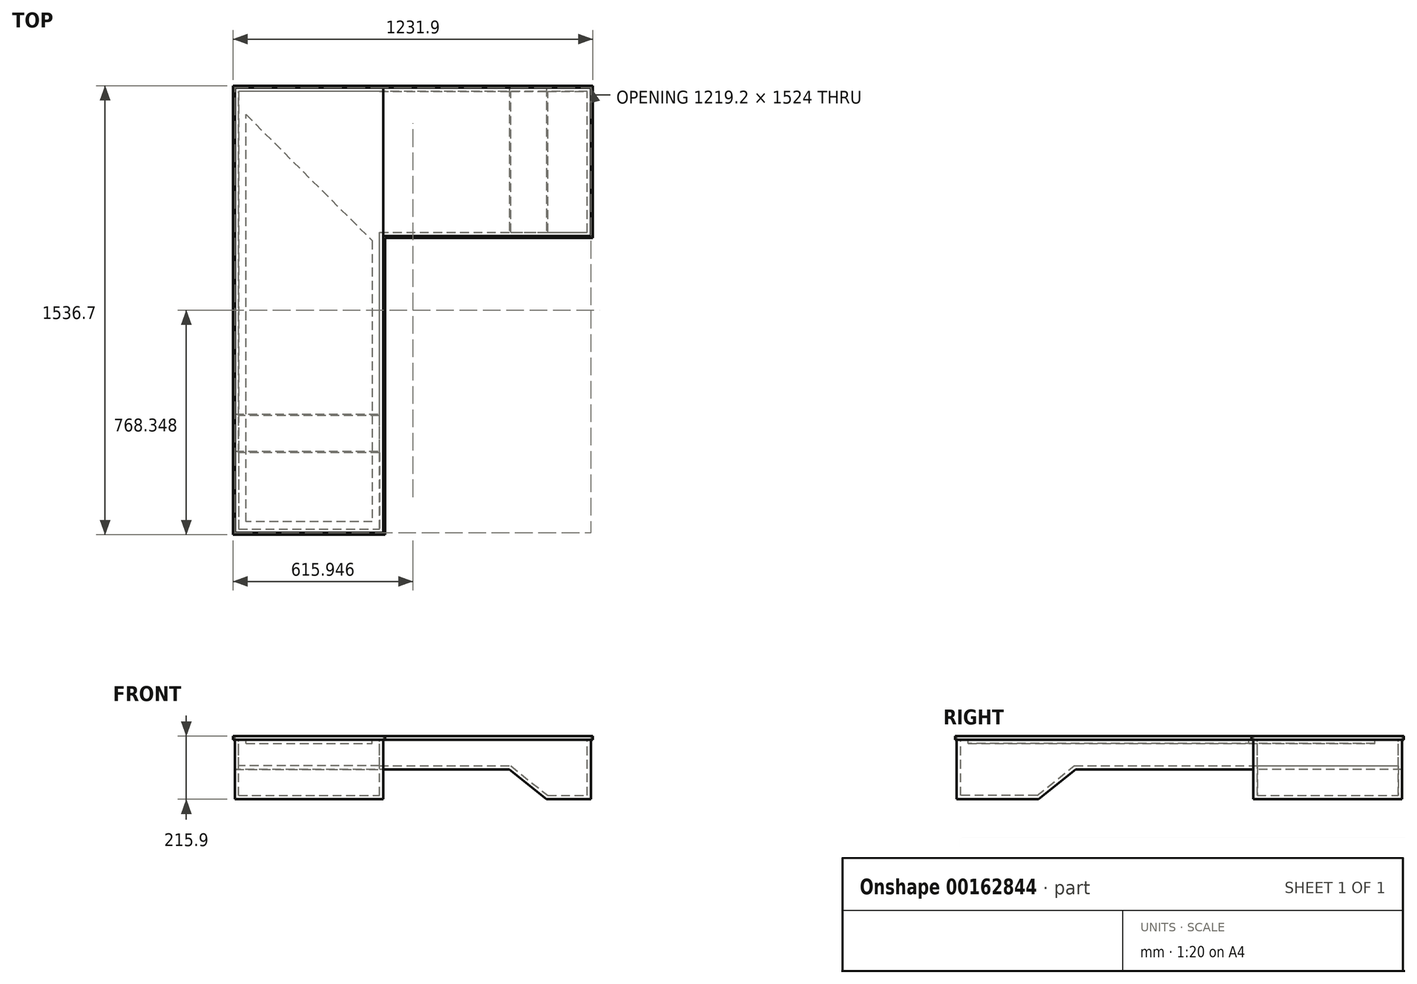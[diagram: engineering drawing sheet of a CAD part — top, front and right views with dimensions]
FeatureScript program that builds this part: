
annotation { "Feature Type Name" : "Feature", "Feature Type Description" : "" }
export const myFeature = defineFeature(function(context is Context, id is Id, definition is map)
    precondition{}
    {
        {
            var Q0;
            Q0=qCreatedBy(makeId("Top.planeOp"),FACE);
            var sketch = newSketch(context, id + "F0", { "sketchPlane" : qUnion([Q0])});
            skLineSegment(sketch, "E0.bottom", {"start": v(-651, 925.2) * mm, "end": v(-143, 925.2) * mm});
            skLineSegment(sketch, "E0.top", {"start": v(-651, -598.8) * mm, "end": v(-143, -598.8) * mm});
            skLineSegment(sketch, "E0.left", {"start": v(-651, 925.2) * mm, "end": v(-651, -598.8) * mm});
            skLineSegment(sketch, "E1.bottom", {"start": v(-143, 925.2) * mm, "end": v(568.2, 925.2) * mm});
            skLineSegment(sketch, "E1.top", {"start": v(-143, 417.2) * mm, "end": v(568.2, 417.2) * mm});
            skLineSegment(sketch, "E1.right", {"start": v(568.2, 925.2) * mm, "end": v(568.2, 417.2) * mm});
            skPoint(sketch, "E2", {"position": v(-143, 417.2) * mm});
            skPoint(sketch, "E3", {"position": v(-143, 925.2) * mm});
            skLineSegment(sketch, "E4", {"start": v(-143, 417.2) * mm, "end": v(-143, -598.8) * mm});
            skSolve(sketch);
        }
        {
            var Q0;
            Q0 = qSketchRegion(id + "F0", true);
            var Q1;
            Q1=makeQuery(id+"F0.imprint","IMPRINT",FACE,{"disambiguationData":[TD([[makeQuery(id+"F0.imprint","IMPRINT",EDGE,{"derivedFrom":sQuery(id+"F0.wireOp",EDGE,"E0.bottom")}),-1.0]])]});
            extrude(context, id + "F1", {"entities" : qUnion([Q0, Q1]), "depth" : 203.2 * mm});
        }
        {
            var Q0;
            Q0=makeQuery(id+"F1.opExtrude","SWEPT_FACE",FACE,{"disambiguationData":[OSD([sQuery(id+"F0.wireOp",EDGE,"E4")])]});
            var sketch = newSketch(context, id + "F2", { "sketchPlane" : qUnion([Q0])});
            skLineSegment(sketch, "E5", {"start": v(-319.4, 0) * mm, "end": v(-192.4, 101.6) * mm});
            skLineSegment(sketch, "E6", {"start": v(-192.4, 101.6) * mm, "end": v(417.2, 101.6) * mm});
            skPoint(sketch, "E6.endSnap0", {"position": v(417.2, 101.6) * mm});
            skSolve(sketch);
        }
        {
            var Q0;
            {var subQ0=sQuery(id+"F2.wireOp",EDGE,"E5");Q0=makeQuery(id+"F2.imprint","IMPRINT",FACE,{"disambiguationData":[TD([[makeQuery(id+"F2.imprint","IMPRINT",EDGE,{"derivedFrom":subQ0}),-1.0]])]});}
            var Q1;
            Q1=makeQuery(id+"F1.opExtrude","SWEPT_FACE",FACE,{"disambiguationData":[OSD([sQuery(id+"F0.wireOp",EDGE,"E0.left")])]});
            extrude(context, id + "F3", {"entities" : qUnion([Q0]), "operationType" : NewBodyOperationType.REMOVE, "endBound" : BoundingType.UP_TO_SURFACE, "oppositeDirection" : true, "endBoundEntityFace" : qUnion([Q1]), "depth" : 25.4 * mm});
        }
        {
            var Q0;
            {var subQ0=sQuery(id+"F0.wireOp",EDGE,"E1.top");Q0=makeQuery(id+"F3.boolean.opBoolean","MERGE",FACE,{"derivedFrom":[makeQuery(id+"F1.opExtrude","SWEPT_FACE",FACE,{"disambiguationData":[OSD([subQ0])]}),makeQuery(id+"F3.opExtrude","SWEPT_FACE",FACE,{"disambiguationData":[OSD([subQ0,sQuery(id+"F0.wireOp",EDGE,"E4")])]})]});}
            var sketch = newSketch(context, id + "F4", { "sketchPlane" : qUnion([Q0])});
            skLineSegment(sketch, "E7", {"start": v(-143, 101.6) * mm, "end": v(288.8, 101.6) * mm});
            skLineSegment(sketch, "E8", {"start": v(288.8, 101.6) * mm, "end": v(415.8, 0) * mm});
            skSolve(sketch);
        }
        {
            var Q0;
            Q0=makeQuery(id+"F4.imprint","IMPRINT",FACE,{"disambiguationData":[TD([[makeQuery(id+"F4.imprint","IMPRINT",EDGE,{"derivedFrom":sQuery(id+"F4.wireOp",EDGE,"E7")}),-1.0]])]});
            extrude(context, id + "F5", {"entities" : qUnion([Q0]), "operationType" : NewBodyOperationType.REMOVE, "oppositeDirection" : true, "depth" : 533.4 * mm});
        }
        {
            var Q0;
            Q0=makeQuery(id+"F1.opExtrude","CAP_FACE",FACE,{"disambiguationData":[OSD([sQuery(id+"F0.wireOp",EDGE,"E0.bottom"),sQuery(id+"F0.wireOp",EDGE,"E0.top"),sQuery(id+"F0.wireOp",EDGE,"E0.left"),sQuery(id+"F0.wireOp",EDGE,"E1.bottom"),sQuery(id+"F0.wireOp",EDGE,"E1.top"),sQuery(id+"F0.wireOp",EDGE,"E1.right"),sQuery(id+"F0.wireOp",EDGE,"E4")])],"isStart":false});
            var sketch = newSketch(context, id + "F6", { "sketchPlane" : qUnion([Q0])});
            skLineSegment(sketch, "E9.0", {"start": v(555.5, 429.9) * mm, "end": v(555.5, 912.5) * mm});
            skLineSegment(sketch, "E9.1", {"start": v(-638.3, 912.5) * mm, "end": v(-638.3, -586.1) * mm});
            skLineSegment(sketch, "E9.2", {"start": v(-638.3, -586.1) * mm, "end": v(-155.7, -586.1) * mm});
            skLineSegment(sketch, "E9.3", {"start": v(555.5, 912.5) * mm, "end": v(-638.3, 912.5) * mm});
            skLineSegment(sketch, "E9.4", {"start": v(-155.7, -586.1) * mm, "end": v(-155.7, 429.9) * mm});
            skLineSegment(sketch, "E9.5", {"start": v(-155.7, 429.9) * mm, "end": v(555.5, 429.9) * mm});
            skSolve(sketch);
        }
        {
            var Q0;
            Q0=makeQuery(id+"F6.imprint","IMPRINT",FACE,{"disambiguationData":[TD([[makeQuery(id+"F6.imprint","IMPRINT",EDGE,{"derivedFrom":sQuery(id+"F6.wireOp",EDGE,"E9.0")}),1.0]])]});
            var sketch = newSketch(context, id + "F7", { "sketchPlane" : qUnion([Q0])});
            skLineSegment(sketch, "E10.5", {"start": v(-644.64, -592.45) * mm, "end": v(-149.34, -592.45) * mm});
            skLineSegment(sketch, "E11", {"start": v(-155.7, 429.9) * mm, "end": v(-638.3, 912.5) * mm});
            skSolve(sketch);
        }
        {
            var Q0;
            Q0=makeQuery(id+"F7.imprint","IMPRINT",FACE,{"disambiguationData":[TD([[makeQuery(id+"F7.imprint","IMPRINT",EDGE,{"derivedFrom":sQuery(id+"F7.wireOp",EDGE,"E11")}),1.0]])]});
            extrude(context, id + "F8", {"entities" : qUnion([Q0]), "operationType" : NewBodyOperationType.REMOVE, "oppositeDirection" : true, "depth" : 501.65 * mm});
        }
        {
            var Q0;
            Q0=makeQuery(id+"F6.imprint","IMPRINT",FACE,{"disambiguationData":[TD([[makeQuery(id+"F6.imprint","IMPRINT",EDGE,{"derivedFrom":sQuery(id+"F6.wireOp",EDGE,"E9.0")}),1.0]])]});
            extrude(context, id + "F9", {"entities" : qUnion([Q0]), "operationType" : NewBodyOperationType.REMOVE, "oppositeDirection" : true, "depth" : 203.2 * mm});
        }
        {
            var Q0;
            Q0=makeQuery(id+"F8.boolean.opBoolean","COPY",FACE,{"derivedFrom":makeQuery(id+"F8.opExtrude","SWEPT_FACE",FACE,{"disambiguationData":[OSD([sQuery(id+"F6.wireOp",EDGE,"E9.1")])]})});
            var sketch = newSketch(context, id + "F10", { "sketchPlane" : qUnion([Q0])});
            skLineSegment(sketch, "E12.0", {"start": v(-573.4, 12.7) * mm, "end": v(-323.86, 12.7) * mm});
            skLineSegment(sketch, "E12.1", {"start": v(-196.86, 114.3) * mm, "end": v(899.8, 114.3) * mm});
            skLineSegment(sketch, "E12.3", {"start": v(-323.86, 12.7) * mm, "end": v(-196.86, 114.3) * mm});
            skLineSegment(sketch, "E13", {"start": v(899.8, 114.3) * mm, "end": v(912.5, 114.3) * mm});
            skLineSegment(sketch, "E14", {"start": v(-573.4, 12.7) * mm, "end": v(-586.1, 12.7) * mm});
            skSolve(sketch);
        }
        {
            var Q0;
            {var subQ0=sQuery(id+"F0.wireOp",EDGE,"E0.top");var subQ1=sQuery(id+"F0.wireOp",EDGE,"E0.left");var subQ2=sQuery(id+"F0.wireOp",EDGE,"E4");Q0=makeQuery(id+"F3.boolean.opBoolean","SPLIT",FACE,{"disambiguationData":[TD([makeQuery(id+"F1.opExtrude","SWEPT_FACE",FACE,{"disambiguationData":[OSD([subQ0])]})])],"derivedFrom":makeQuery(id+"F1.opExtrude","CAP_FACE",FACE,{"disambiguationData":[OSD([sQuery(id+"F0.wireOp",EDGE,"E0.bottom"),subQ0,subQ1,sQuery(id+"F0.wireOp",EDGE,"E1.bottom"),sQuery(id+"F0.wireOp",EDGE,"E1.top"),sQuery(id+"F0.wireOp",EDGE,"E1.right"),subQ2])],"isStart":true})});}
            var sketch = newSketch(context, id + "F11", { "sketchPlane" : qUnion([Q0])});
            skLineSegment(sketch, "E15", {"start": v(-155.7, 319.4) * mm, "end": v(-638.3, 319.4) * mm});
            skSolve(sketch);
        }
        {
            var Q0;
            Q0 = qSketchRegion(id + "F11", true);
            var Q1;
            Q1=makeQuery(id+"F11.imprint","IMPRINT",FACE,{"disambiguationData":[TD([[makeQuery(id+"F11.imprint","IMPRINT",EDGE,{"derivedFrom":sQuery(id+"F11.wireOp",EDGE,"E15")}),-1.0]])]});
            extrude(context, id + "F12", {"entities" : qUnion([Q0, Q1]), "operationType" : NewBodyOperationType.ADD, "oppositeDirection" : true, "depth" : 12.7 * mm});
        }
        {
            var Q0;
            Q0=makeQuery(id+"F10.imprint","IMPRINT",FACE,{"disambiguationData":[TD([[makeQuery(id+"F10.imprint","IMPRINT",EDGE,{"derivedFrom":sQuery(id+"F10.wireOp",EDGE,"E12.0")}),-1.0]])]});
            var sketch = newSketch(context, id + "F13", { "sketchPlane" : qUnion([Q0])});
            skSolve(sketch);
        }
        {
            var Q0;
            Q0 = qSketchRegion(id + "F13", true);
            var Q1;
            Q1=makeQuery(id+"F10.imprint","IMPRINT",FACE,{"disambiguationData":[TD([[makeQuery(id+"F10.imprint","IMPRINT",EDGE,{"derivedFrom":sQuery(id+"F10.wireOp",EDGE,"E12.0")}),-1.0]])]});
            extrude(context, id + "F14", {"entities" : qUnion([Q0, Q1]), "operationType" : NewBodyOperationType.ADD, "depth" : 482.6 * mm});
        }
        {
            var Q0;
            Q0=makeQuery(id+"F9.boolean.opBoolean","COPY",FACE,{"derivedFrom":makeQuery(id+"F9.opExtrude","SWEPT_FACE",FACE,{"disambiguationData":[OSD([sQuery(id+"F6.wireOp",EDGE,"E9.3")])]})});
            var sketch = newSketch(context, id + "F15", { "sketchPlane" : qUnion([Q0])});
            skLineSegment(sketch, "E16.6", {"start": v(293.26, 114.3) * mm, "end": v(420.26, 12.7) * mm});
            skLineSegment(sketch, "E16.7", {"start": v(420.26, 12.7) * mm, "end": v(542.8, 12.7) * mm});
            skLineSegment(sketch, "E17", {"start": v(542.8, 12.7) * mm, "end": v(555.5, 12.7) * mm});
            skLineSegment(sketch, "E18", {"start": v(-155.7, 114.3) * mm, "end": v(293.26, 114.3) * mm});
            skSolve(sketch);
        }
        {
            var Q0;
            Q0 = qSketchRegion(id + "F15", true);
            var Q1;
            Q1=makeQuery(id+"F15.imprint","IMPRINT",FACE,{"disambiguationData":[TD([[makeQuery(id+"F15.imprint","IMPRINT",EDGE,{"derivedFrom":sQuery(id+"F15.wireOp",EDGE,"E16.6")}),-1.0]])]});
            extrude(context, id + "F16", {"entities" : qUnion([Q0, Q1]), "operationType" : NewBodyOperationType.ADD, "depth" : 482.6 * mm});
        }
        {
            var Q0;
            Q0=makeQuery(id+"F1.opExtrude","CAP_FACE",FACE,{"disambiguationData":[OSD([sQuery(id+"F0.wireOp",EDGE,"E0.bottom"),sQuery(id+"F0.wireOp",EDGE,"E0.top"),sQuery(id+"F0.wireOp",EDGE,"E0.left"),sQuery(id+"F0.wireOp",EDGE,"E1.bottom"),sQuery(id+"F0.wireOp",EDGE,"E1.top"),sQuery(id+"F0.wireOp",EDGE,"E1.right"),sQuery(id+"F0.wireOp",EDGE,"E4")])],"isStart":false});
            var sketch = newSketch(context, id + "F17", { "sketchPlane" : qUnion([Q0])});
            skLineSegment(sketch, "E19", {"start": v(-657.34, 931.55) * mm, "end": v(-657.34, -605.15) * mm});
            skLineSegment(sketch, "E20", {"start": v(574.56, 410.85) * mm, "end": v(574.56, 931.55) * mm});
            skLineSegment(sketch, "E21", {"start": v(-657.34, 931.55) * mm, "end": v(574.56, 931.55) * mm});
            skLineSegment(sketch, "E22", {"start": v(-136.64, 410.85) * mm, "end": v(574.56, 410.85) * mm});
            skLineSegment(sketch, "E23", {"start": v(-136.64, -605.15) * mm, "end": v(-136.64, 410.85) * mm});
            skLineSegment(sketch, "E24", {"start": v(-657.34, -605.15) * mm, "end": v(-136.64, -605.15) * mm});
            skSolve(sketch);
        }
        {
            var Q0;
            Q0=makeQuery(id+"F17.imprint","IMPRINT",FACE,{"disambiguationData":[TD([[makeQuery(id+"F17.imprint","IMPRINT",EDGE,{"derivedFrom":sQuery(id+"F17.wireOp",EDGE,"E19")}),1.0]])]});
            extrude(context, id + "F18", {"entities" : qUnion([Q0]), "depth" : 12.7 * mm});
        }
        {
            var Q0;
            Q0=makeQuery(id+"F18.opExtrude","SWEPT_FACE",FACE,{"disambiguationData":[OSD([sQuery(id+"F0.wireOp",EDGE,"E1.top")])]});
            var sketch = newSketch(context, id + "F19", { "sketchPlane" : qUnion([Q0])});
            skSolve(sketch);
        }
        {
            var Q0;
            Q0 = qSketchRegion(id + "F19", true);
            var Q1;
            {var subQ0=sQuery(id+"F0.wireOp",EDGE,"E1.top");Q1=makeQuery(id+"F19.imprint","IMPRINT",FACE,{"disambiguationData":[TD([[makeQuery(id+"F19.imprint","IMPRINT",EDGE,{"derivedFrom":makeQuery(id+"F18.opExtrude","CAP_EDGE",EDGE,{"disambiguationData":[OSD([subQ0])],"isStart":true})}),-1.0]])]});}
            extrude(context, id + "F20", {"entities" : qUnion([Q0, Q1]), "depth" : 508 * mm});
        }
        {
            var Q0;
            Q0=makeQuery(id+"F18.opExtrude","SWEPT_FACE",FACE,{"disambiguationData":[OSD([sQuery(id+"F0.wireOp",EDGE,"E0.left")])]});
            var sketch = newSketch(context, id + "F21", { "sketchPlane" : qUnion([Q0])});
            skSolve(sketch);
        }
        {
            var Q0;
            {var subQ0=sQuery(id+"F0.wireOp",EDGE,"E0.left");Q0=makeQuery(id+"F21.imprint","IMPRINT",FACE,{"disambiguationData":[TD([[makeQuery(id+"F21.imprint","IMPRINT",EDGE,{"derivedFrom":makeQuery(id+"F18.opExtrude","CAP_EDGE",EDGE,{"disambiguationData":[OSD([subQ0])],"isStart":true})}),-1.0]])]});}
            var sketch = newSketch(context, id + "F22", { "sketchPlane" : qUnion([Q0])});
            skSolve(sketch);
        }
        {
            var Q0;
            Q0 = qSketchRegion(id + "F22", true);
            var Q1;
            {var subQ0=sQuery(id+"F0.wireOp",EDGE,"E0.left");Q1=makeQuery(id+"F21.imprint","IMPRINT",FACE,{"disambiguationData":[TD([[makeQuery(id+"F21.imprint","IMPRINT",EDGE,{"derivedFrom":makeQuery(id+"F18.opExtrude","CAP_EDGE",EDGE,{"disambiguationData":[OSD([subQ0])],"isStart":true})}),-1.0]])]});}
            extrude(context, id + "F23", {"entities" : qUnion([Q0, Q1]), "depth" : 508 * mm});
        }
        {
            var Q0;
            {var subQ0=sQuery(id+"F0.wireOp",EDGE,"E0.left");Q0=makeQuery(id+"F23.opExtrude","SWEPT_FACE",FACE,{"disambiguationData":[OSD([subQ0]),TDD([makeQuery(id+"F21.imprint","IMPRINT",EDGE,{"derivedFrom":makeQuery(id+"F18.opExtrude","CAP_EDGE",EDGE,{"disambiguationData":[OSD([subQ0])],"isStart":false})})])]});}
            var sketch = newSketch(context, id + "F24", { "sketchPlane" : qUnion([Q0])});
            skLineSegment(sketch, "E25", {"start": v(-651, 925.2) * mm, "end": v(-143, 417.2) * mm});
            skSolve(sketch);
        }
        {
            var Q0;
            {var subQ0=sQuery(id+"F24.wireOp",EDGE,"E25");Q0=makeQuery(id+"F24.imprint","IMPRINT",FACE,{"disambiguationData":[TD([[makeQuery(id+"F24.imprint","IMPRINT",EDGE,{"derivedFrom":subQ0}),-1.0]])]});}
            var sketch = newSketch(context, id + "F25", { "sketchPlane" : qUnion([Q0])});
            skLineSegment(sketch, "E26.0", {"start": v(-168.4, 406.68) * mm, "end": v(-625.6, 863.88) * mm});
            skLineSegment(sketch, "E26.1", {"start": v(-168.4, -573.4) * mm, "end": v(-168.4, 406.68) * mm});
            skLineSegment(sketch, "E26.2", {"start": v(-625.6, -573.4) * mm, "end": v(-168.4, -573.4) * mm});
            skLineSegment(sketch, "E26.3", {"start": v(-625.6, 863.88) * mm, "end": v(-625.6, -573.4) * mm});
            skSolve(sketch);
        }
        {
            var Q0;
            Q0=makeQuery(id+"F25.imprint","IMPRINT",FACE,{"disambiguationData":[TD([[makeQuery(id+"F25.imprint","IMPRINT",EDGE,{"derivedFrom":sQuery(id+"F25.wireOp",EDGE,"E26.0")}),1.0]])]});
            var sketch = newSketch(context, id + "F26", { "sketchPlane" : qUnion([Q0])});
            skLineSegment(sketch, "E27.0", {"start": v(-181.1, -560.7) * mm, "end": v(-181.1, 401.42) * mm});
            skLineSegment(sketch, "E27.1", {"start": v(-612.9, -560.7) * mm, "end": v(-181.1, -560.7) * mm});
            skLineSegment(sketch, "E27.2", {"start": v(-612.9, 833.22) * mm, "end": v(-612.9, -560.7) * mm});
            skLineSegment(sketch, "E27.3", {"start": v(-181.1, 401.42) * mm, "end": v(-612.9, 833.22) * mm});
            skSolve(sketch);
        }
        {
            var Q0;
            Q0 = qSketchRegion(id + "F26", true);
            extrude(context, id + "F27", {"entities" : qUnion([Q0]), "operationType" : NewBodyOperationType.ADD, "oppositeDirection" : true, "depth" : 3.17 * mm});
        }
        {
            var Q0;
            Q0=makeQuery(id+"F26.imprint","IMPRINT",FACE,{"disambiguationData":[TD([[makeQuery(id+"F26.imprint","IMPRINT",EDGE,{"derivedFrom":sQuery(id+"F26.wireOp",EDGE,"E27.0")}),1.0]])]});
            var sketch = newSketch(context, id + "F28", { "sketchPlane" : qUnion([Q0])});
            skSolve(sketch);
        }
        {
            var Q0;
            Q0=makeQuery(id+"F28.imprint","IMPRINT",FACE,{"disambiguationData":[TD([[makeQuery(id+"F28.imprint","IMPRINT",EDGE,{"derivedFrom":makeQuery(id+"F26.imprint","IMPRINT",EDGE,{"derivedFrom":sQuery(id+"F26.wireOp",EDGE,"E27.0")})}),1.0]])]});
            extrude(context, id + "F29", {"entities" : qUnion([Q0]), "operationType" : NewBodyOperationType.ADD, "oppositeDirection" : true, "depth" : 25.4 * mm});
        }
        {
            var Q0;
            Q0=makeQuery(id+"F26.imprint","IMPRINT",FACE,{"disambiguationData":[TD([[makeQuery(id+"F26.imprint","IMPRINT",EDGE,{"derivedFrom":sQuery(id+"F26.wireOp",EDGE,"E27.0")}),1.0]])]});
            extrude(context, id + "F30", {"entities" : qUnion([Q0]), "operationType" : NewBodyOperationType.ADD, "oppositeDirection" : true, "depth" : 12.7 * mm});
        }
    });
